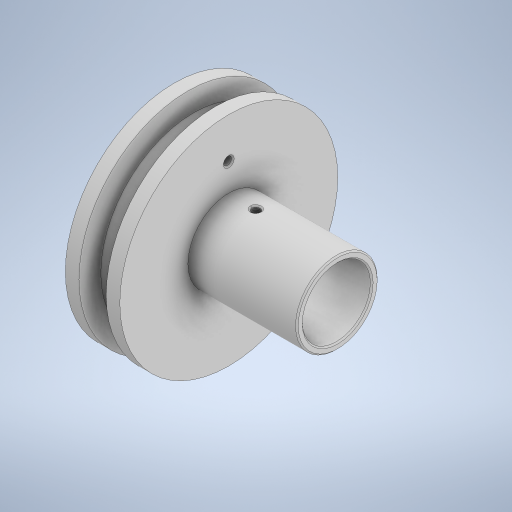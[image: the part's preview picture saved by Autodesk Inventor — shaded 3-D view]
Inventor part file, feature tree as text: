
AUTODESK INVENTOR PART (.ipt)
format: ipt  version: 2023 (Build 270158000, 158)  size: 344,064 bytes
history: native  units: mm
features: sketch x6, chamfer x5, extrude x4, other x3, revolve x1, thread x1
ambient origin geometry x8: Origin, YZ Plane, XZ Plane, XY Plane, X Axis, Y Axis, Z Axis, Center Point
bodies: Body1 (feature_tree)
feature tree (20):
  other  "Твердое тело1"
  revolve  "Вращение1"
  extrude  "Выдавливание1"  Depth=20.0mm
  extrude  "Выдавливание2"  Depth=40.0mm
  chamfer  "Фаска1"  Distance=7.0mm
  chamfer  "Фаска2"  Distance=6.0mm
  sketch  "Эскиз4"
  other  "РабПлоскость1"
  extrude  "Выдавливание3"  Depth=6.0mm
  thread  "Резьба1"
  chamfer  "Фаска3"  Angle=90.0deg  [1 undecoded]
  other  "РабПлоскость2"
  extrude  "Выдавливание4"  Depth=30.0mm
  chamfer  "Фаска4"  Distance=40.0mm
  chamfer  "Фаска5"  Distance=25.0mm
  sketch  "Эскиз1"
  sketch  "Эскиз2"
  sketch  "Эскиз3"
  sketch  "Эскиз5"
  sketch  "Эскиз6"
note: 1 required parameter value undecoded (feature->parameter linkage not recoverable at this tier; creation-order binding heuristic only, values carry confidence <= 0.55)
